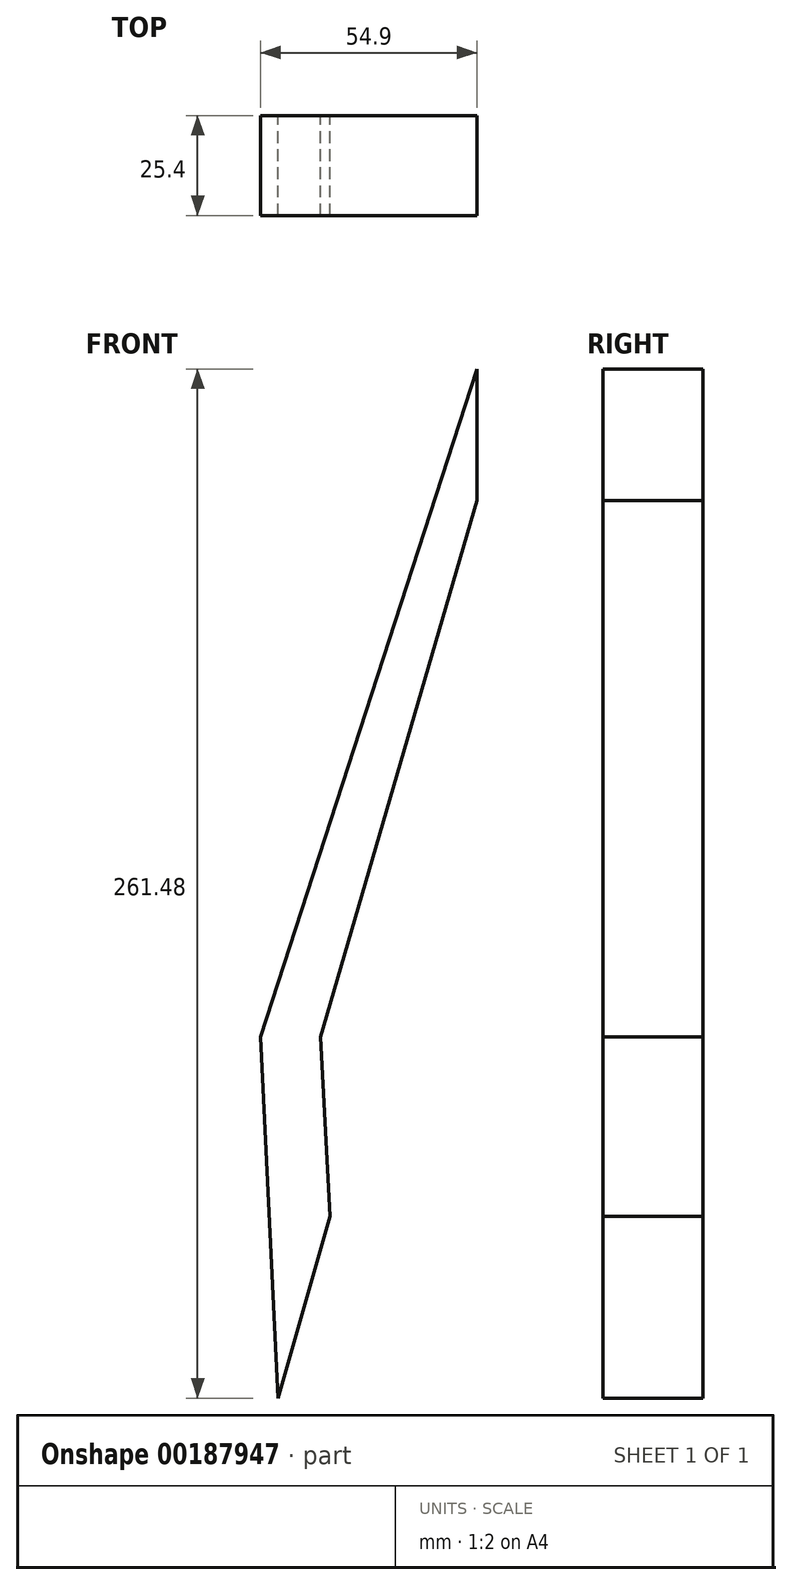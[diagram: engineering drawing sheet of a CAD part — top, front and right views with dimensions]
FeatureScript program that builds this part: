
annotation { "Feature Type Name" : "Feature", "Feature Type Description" : "" }
export const myFeature = defineFeature(function(context is Context, id is Id, definition is map)
    precondition{}
    {
        {
            var Q0;
            Q0=qCreatedBy(makeId("Front.planeOp"),FACE);
            var sketch = newSketch(context, id + "F0", { "sketchPlane" : qUnion([Q0])});
            skLineSegment(sketch, "E0", {"start": v(25.18, 124.61) * mm, "end": v(25.18, 91.14) * mm});
            skLineSegment(sketch, "E1", {"start": v(25.18, 91.14) * mm, "end": v(-14.54, -45.06) * mm});
            skLineSegment(sketch, "E2", {"start": v(-14.54, -45.06) * mm, "end": v(-12.1, -90.7) * mm});
            skLineSegment(sketch, "E3", {"start": v(-12.1, -90.7) * mm, "end": v(-25.31, -136.87) * mm});
            skLineSegment(sketch, "E4", {"start": v(-25.31, -136.87) * mm, "end": v(-29.72, -45.06) * mm});
            skLineSegment(sketch, "E5", {"start": v(-29.72, -45.06) * mm, "end": v(25.18, 124.61) * mm});
            skSolve(sketch);
        }
        {
            var Q0;
            Q0=makeQuery(id+"F0.imprint","IMPRINT",FACE,{"disambiguationData":[TD([[makeQuery(id+"F0.imprint","IMPRINT",EDGE,{"derivedFrom":sQuery(id+"F0.wireOp",EDGE,"E0")}),-1.0]])]});
            extrude(context, id + "F1", {"entities" : qUnion([Q0]), "depth" : 25.4 * mm});
        }
    });
